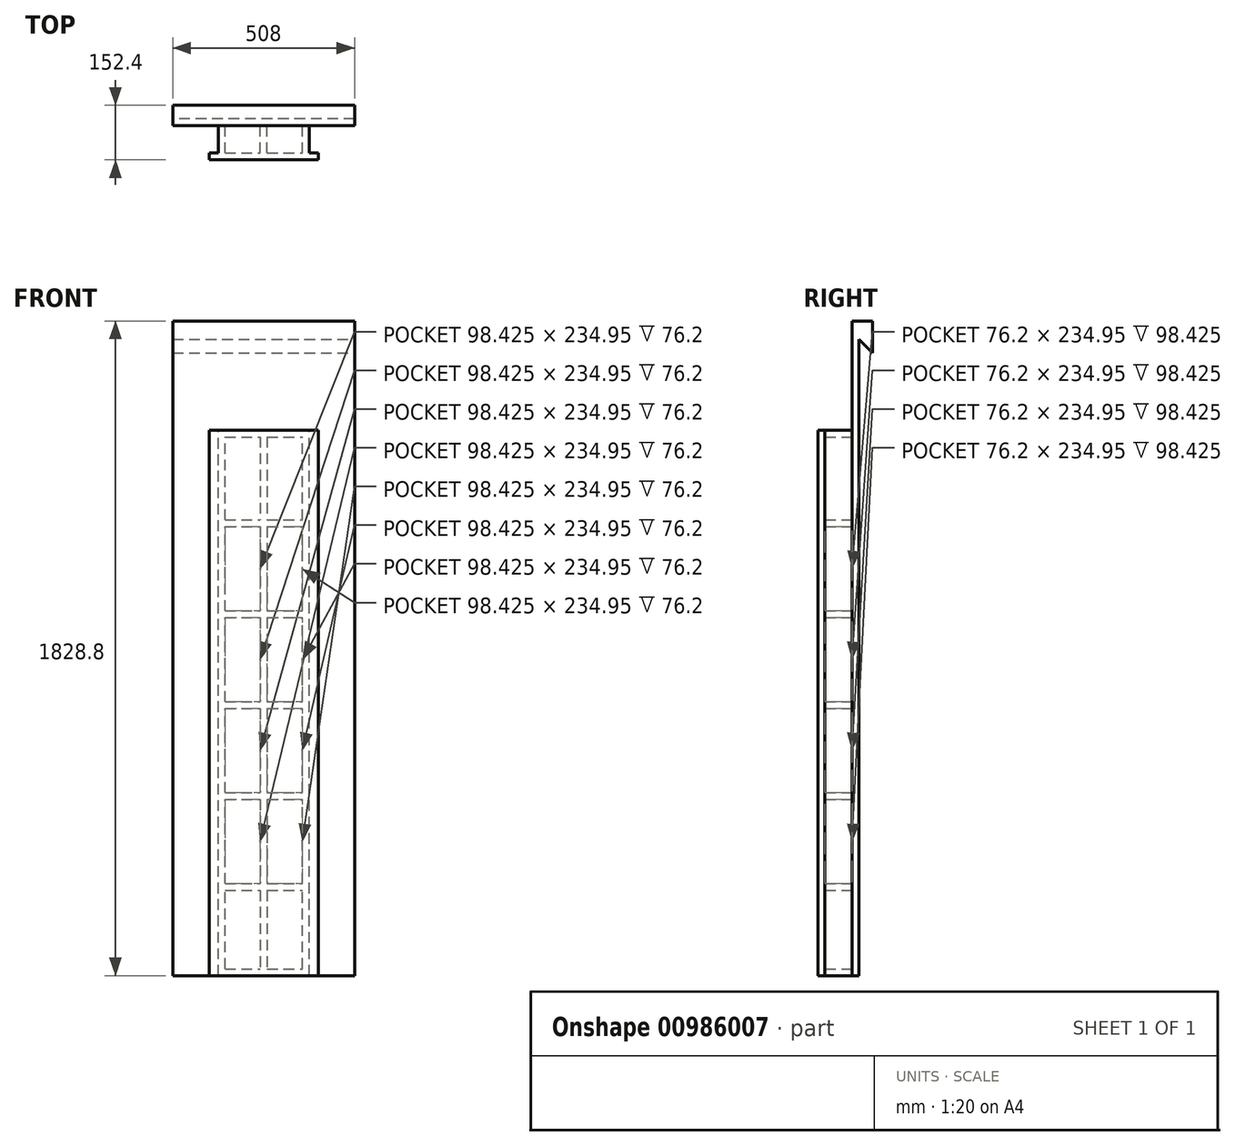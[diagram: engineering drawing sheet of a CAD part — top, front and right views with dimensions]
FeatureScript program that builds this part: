
annotation { "Feature Type Name" : "Feature", "Feature Type Description" : "" }
export const myFeature = defineFeature(function(context is Context, id is Id, definition is map)
    precondition{}
    {
        {
            var Q0;
            Q0=qCreatedBy(makeId("Front.planeOp"),FACE);
            var sketch = newSketch(context, id + "F0", { "sketchPlane" : qUnion([Q0])});
            skLineSegment(sketch, "E0.bottom", {"start": v(254, 914.4) * mm, "end": v(-254, 914.4) * mm});
            skLineSegment(sketch, "E0.top", {"start": v(254, -914.4) * mm, "end": v(-254, -914.4) * mm});
            skLineSegment(sketch, "E0.left", {"start": v(254, 914.4) * mm, "end": v(254, -914.4) * mm});
            skLineSegment(sketch, "E0.right", {"start": v(-254, 914.4) * mm, "end": v(-254, -914.4) * mm});
            skPoint(sketch, "E0.middle", {"position": v(0, 0) * mm});
            skSolve(sketch);
        }
        {
            var Q0;
            Q0=makeQuery(id+"F0.imprint","IMPRINT",FACE,{"disambiguationData":[TD([[makeQuery(id+"F0.imprint","IMPRINT",EDGE,{"derivedFrom":sQuery(id+"F0.wireOp",EDGE,"E0.bottom")}),1.0]])]});
            extrude(context, id + "F1", {"entities" : qUnion([Q0]), "depth" : 19.05 * mm, "offsetDistance" : 25.4 * mm});
        }
        {
            var Q0;
            Q0=makeQuery(id+"F1.opExtrude","CAP_FACE",FACE,{"disambiguationData":[OSD([sQuery(id+"F0.wireOp",EDGE,"E0.bottom"),sQuery(id+"F0.wireOp",EDGE,"E0.top"),sQuery(id+"F0.wireOp",EDGE,"E0.left"),sQuery(id+"F0.wireOp",EDGE,"E0.right")])],"isStart":false});
            var sketch = newSketch(context, id + "F2", { "sketchPlane" : qUnion([Q0])});
            skLineSegment(sketch, "E1.bottom", {"start": v(-127, -914.4) * mm, "end": v(127, -914.4) * mm});
            skLineSegment(sketch, "E1.top", {"start": v(-127, 609.6) * mm, "end": v(127, 609.6) * mm});
            skLineSegment(sketch, "E1.left", {"start": v(-127, -914.4) * mm, "end": v(-127, 609.6) * mm});
            skLineSegment(sketch, "E1.right", {"start": v(127, -914.4) * mm, "end": v(127, 609.6) * mm});
            skLineSegment(sketch, "E2.bottom", {"start": v(9.52, 609.6) * mm, "end": v(-9.53, 609.6) * mm});
            skLineSegment(sketch, "E2.top", {"start": v(9.52, -914.4) * mm, "end": v(-9.53, -914.4) * mm});
            skLineSegment(sketch, "E2.left", {"start": v(9.52, 590.55) * mm, "end": v(9.52, 358.78) * mm});
            skLineSegment(sketch, "E2.right", {"start": v(-9.53, 590.55) * mm, "end": v(-9.53, 358.78) * mm});
            skPoint(sketch, "E2.middle", {"position": v(0, -152.4) * mm});
            skPoint(sketch, "E2.middle.positionSnap0", {"position": v(127, -152.4) * mm});
            skPoint(sketch, "E2.centerSnap0", {"position": v(127, -152.4) * mm});
            skLineSegment(sketch, "E3.0", {"start": v(-107.95, -895.35) * mm, "end": v(-107.95, -676.28) * mm});
            skLineSegment(sketch, "E3.1", {"start": v(-107.95, -895.35) * mm, "end": v(-9.53, -895.35) * mm});
            skLineSegment(sketch, "E3.2", {"start": v(107.95, -895.35) * mm, "end": v(107.95, -676.28) * mm});
            skLineSegment(sketch, "E3.3", {"start": v(-107.95, 590.55) * mm, "end": v(-9.53, 590.55) * mm});
            skLineSegment(sketch, "E4.bottom", {"start": v(-107.95, 358.78) * mm, "end": v(-9.53, 358.78) * mm});
            skLineSegment(sketch, "E4.top", {"start": v(-107.95, 339.73) * mm, "end": v(-9.53, 339.73) * mm});
            skLineSegment(sketch, "E5.bottom", {"start": v(-107.95, 104.78) * mm, "end": v(-9.53, 104.78) * mm});
            skLineSegment(sketch, "E5.top", {"start": v(-107.95, 85.73) * mm, "end": v(-9.53, 85.73) * mm});
            skLineSegment(sketch, "E6.bottom", {"start": v(-107.95, -149.23) * mm, "end": v(-9.53, -149.23) * mm});
            skLineSegment(sketch, "E6.top", {"start": v(-107.95, -168.28) * mm, "end": v(-9.53, -168.28) * mm});
            skLineSegment(sketch, "E7.bottom", {"start": v(-107.95, -403.23) * mm, "end": v(-9.53, -403.23) * mm});
            skLineSegment(sketch, "E7.top", {"start": v(-107.95, -422.28) * mm, "end": v(-9.53, -422.28) * mm});
            skLineSegment(sketch, "E8.bottom", {"start": v(-107.95, -676.28) * mm, "end": v(-9.53, -676.28) * mm});
            skLineSegment(sketch, "E8.top", {"start": v(-107.95, -657.23) * mm, "end": v(-9.53, -657.23) * mm});
            skLineSegment(sketch, "E9.trimOffspring", {"start": v(9.52, 590.55) * mm, "end": v(107.95, 590.55) * mm});
            skLineSegment(sketch, "E10.trimOffspring", {"start": v(107.95, 358.78) * mm, "end": v(107.95, 590.55) * mm});
            skLineSegment(sketch, "E11.trimOffspring", {"start": v(-107.95, 358.78) * mm, "end": v(-107.95, 590.55) * mm});
            skLineSegment(sketch, "E12.trimOffspring", {"start": v(9.52, 358.78) * mm, "end": v(107.95, 358.78) * mm});
            skLineSegment(sketch, "E13.trimOffspring", {"start": v(9.52, 339.73) * mm, "end": v(9.52, 104.78) * mm});
            skLineSegment(sketch, "E14.trimOffspring", {"start": v(-9.53, 339.73) * mm, "end": v(-9.53, 104.78) * mm});
            skLineSegment(sketch, "E15.trimOffspring", {"start": v(9.52, 339.73) * mm, "end": v(107.95, 339.73) * mm});
            skLineSegment(sketch, "E16.trimOffspring", {"start": v(107.95, 104.78) * mm, "end": v(107.95, 339.73) * mm});
            skLineSegment(sketch, "E17.trimOffspring", {"start": v(9.52, 104.78) * mm, "end": v(107.95, 104.78) * mm});
            skLineSegment(sketch, "E18.trimOffspring", {"start": v(9.52, 85.73) * mm, "end": v(9.52, -149.23) * mm});
            skLineSegment(sketch, "E19.trimOffspring", {"start": v(9.52, 85.73) * mm, "end": v(107.95, 85.73) * mm});
            skLineSegment(sketch, "E20.trimOffspring", {"start": v(-9.53, 85.73) * mm, "end": v(-9.53, -149.23) * mm});
            skLineSegment(sketch, "E21.trimOffspring", {"start": v(-107.95, 104.78) * mm, "end": v(-107.95, 339.73) * mm});
            skLineSegment(sketch, "E22.trimOffspring", {"start": v(107.95, -149.23) * mm, "end": v(107.95, 85.73) * mm});
            skLineSegment(sketch, "E23.trimOffspring", {"start": v(9.52, -168.28) * mm, "end": v(9.52, -403.23) * mm});
            skLineSegment(sketch, "E24.trimOffspring", {"start": v(9.52, -149.23) * mm, "end": v(107.95, -149.23) * mm});
            skLineSegment(sketch, "E25.trimOffspring", {"start": v(-9.53, -168.28) * mm, "end": v(-9.53, -403.23) * mm});
            skLineSegment(sketch, "E26.trimOffspring", {"start": v(9.52, -168.28) * mm, "end": v(107.95, -168.28) * mm});
            skLineSegment(sketch, "E27.trimOffspring", {"start": v(-107.95, -149.23) * mm, "end": v(-107.95, 85.73) * mm});
            skLineSegment(sketch, "E28.trimOffspring", {"start": v(107.95, -403.23) * mm, "end": v(107.95, -168.28) * mm});
            skLineSegment(sketch, "E29.trimOffspring", {"start": v(9.52, -422.28) * mm, "end": v(9.52, -657.23) * mm});
            skLineSegment(sketch, "E30.trimOffspring", {"start": v(9.52, -422.28) * mm, "end": v(107.95, -422.28) * mm});
            skLineSegment(sketch, "E31.trimOffspring", {"start": v(9.52, -403.23) * mm, "end": v(107.95, -403.23) * mm});
            skLineSegment(sketch, "E32.trimOffspring", {"start": v(-9.53, -422.28) * mm, "end": v(-9.53, -657.23) * mm});
            skLineSegment(sketch, "E33.trimOffspring", {"start": v(-107.95, -403.23) * mm, "end": v(-107.95, -168.28) * mm});
            skLineSegment(sketch, "E34.trimOffspring", {"start": v(107.95, -657.23) * mm, "end": v(107.95, -422.28) * mm});
            skLineSegment(sketch, "E35.trimOffspring", {"start": v(9.52, -657.23) * mm, "end": v(107.95, -657.23) * mm});
            skLineSegment(sketch, "E36.trimOffspring", {"start": v(9.52, -676.28) * mm, "end": v(107.95, -676.28) * mm});
            skLineSegment(sketch, "E37.trimOffspring", {"start": v(9.52, -676.28) * mm, "end": v(9.52, -895.35) * mm});
            skLineSegment(sketch, "E38.trimOffspring", {"start": v(-9.53, -676.28) * mm, "end": v(-9.53, -895.35) * mm});
            skLineSegment(sketch, "E39.trimOffspring", {"start": v(-107.95, -657.23) * mm, "end": v(-107.95, -422.28) * mm});
            skLineSegment(sketch, "E40.trimOffspring", {"start": v(9.52, -895.35) * mm, "end": v(107.95, -895.35) * mm});
            skSolve(sketch);
        }
        {
            var Q0;
            {var subQ3=sQuery(id+"F2.wireOp",EDGE,"E1.left");Q0=makeQuery(id+"F2.imprint","IMPRINT",FACE,{"disambiguationData":[TD([[makeQuery(id+"F2.imprint","IMPRINT",EDGE,{"derivedFrom":subQ3}),-1.0]])]});}
            extrude(context, id + "F3", {"entities" : qUnion([Q0]), "operationType" : NewBodyOperationType.ADD, "depth" : 76.2 * mm, "offsetDistance" : 25.4 * mm});
        }
        {
            var Q0;
            Q0=makeQuery(id+"F3.opExtrude","CAP_FACE",FACE,{"disambiguationData":[OSD([sQuery(id+"F2.wireOp",EDGE,"E1.bottom"),sQuery(id+"F2.wireOp",EDGE,"E1.top"),sQuery(id+"F2.wireOp",EDGE,"E1.left"),sQuery(id+"F2.wireOp",EDGE,"E1.right"),sQuery(id+"F2.wireOp",EDGE,"E2.bottom"),sQuery(id+"F2.wireOp",EDGE,"E2.top"),sQuery(id+"F2.wireOp",EDGE,"E2.left"),sQuery(id+"F2.wireOp",EDGE,"E2.right"),sQuery(id+"F2.wireOp",EDGE,"E3.0"),sQuery(id+"F2.wireOp",EDGE,"E3.1"),sQuery(id+"F2.wireOp",EDGE,"E3.2"),sQuery(id+"F2.wireOp",EDGE,"E3.3"),sQuery(id+"F2.wireOp",EDGE,"E4.bottom"),sQuery(id+"F2.wireOp",EDGE,"E4.top"),sQuery(id+"F2.wireOp",EDGE,"E5.bottom"),sQuery(id+"F2.wireOp",EDGE,"E5.top"),sQuery(id+"F2.wireOp",EDGE,"E6.bottom"),sQuery(id+"F2.wireOp",EDGE,"E6.top"),sQuery(id+"F2.wireOp",EDGE,"E7.bottom"),sQuery(id+"F2.wireOp",EDGE,"E7.top"),sQuery(id+"F2.wireOp",EDGE,"E8.bottom"),sQuery(id+"F2.wireOp",EDGE,"E8.top"),sQuery(id+"F2.wireOp",EDGE,"E9.trimOffspring"),sQuery(id+"F2.wireOp",EDGE,"E10.trimOffspring"),sQuery(id+"F2.wireOp",EDGE,"E11.trimOffspring"),sQuery(id+"F2.wireOp",EDGE,"E12.trimOffspring"),sQuery(id+"F2.wireOp",EDGE,"E13.trimOffspring"),sQuery(id+"F2.wireOp",EDGE,"E14.trimOffspring"),sQuery(id+"F2.wireOp",EDGE,"E15.trimOffspring"),sQuery(id+"F2.wireOp",EDGE,"E16.trimOffspring"),sQuery(id+"F2.wireOp",EDGE,"E17.trimOffspring"),sQuery(id+"F2.wireOp",EDGE,"E18.trimOffspring"),sQuery(id+"F2.wireOp",EDGE,"E19.trimOffspring"),sQuery(id+"F2.wireOp",EDGE,"E20.trimOffspring"),sQuery(id+"F2.wireOp",EDGE,"E21.trimOffspring"),sQuery(id+"F2.wireOp",EDGE,"E22.trimOffspring"),sQuery(id+"F2.wireOp",EDGE,"E23.trimOffspring"),sQuery(id+"F2.wireOp",EDGE,"E24.trimOffspring"),sQuery(id+"F2.wireOp",EDGE,"E25.trimOffspring"),sQuery(id+"F2.wireOp",EDGE,"E26.trimOffspring"),sQuery(id+"F2.wireOp",EDGE,"E27.trimOffspring"),sQuery(id+"F2.wireOp",EDGE,"E28.trimOffspring"),sQuery(id+"F2.wireOp",EDGE,"E29.trimOffspring"),sQuery(id+"F2.wireOp",EDGE,"E30.trimOffspring"),sQuery(id+"F2.wireOp",EDGE,"E31.trimOffspring"),sQuery(id+"F2.wireOp",EDGE,"E32.trimOffspring"),sQuery(id+"F2.wireOp",EDGE,"E33.trimOffspring"),sQuery(id+"F2.wireOp",EDGE,"E34.trimOffspring"),sQuery(id+"F2.wireOp",EDGE,"E35.trimOffspring"),sQuery(id+"F2.wireOp",EDGE,"E36.trimOffspring"),sQuery(id+"F2.wireOp",EDGE,"E37.trimOffspring"),sQuery(id+"F2.wireOp",EDGE,"E38.trimOffspring"),sQuery(id+"F2.wireOp",EDGE,"E39.trimOffspring"),sQuery(id+"F2.wireOp",EDGE,"E40.trimOffspring")])],"isStart":false});
            var sketch = newSketch(context, id + "F4", { "sketchPlane" : qUnion([Q0])});
            skLineSegment(sketch, "E41.bottom", {"start": v(-152.4, -914.4) * mm, "end": v(152.4, -914.4) * mm});
            skLineSegment(sketch, "E41.top", {"start": v(-152.4, 609.6) * mm, "end": v(152.4, 609.6) * mm});
            skLineSegment(sketch, "E41.left", {"start": v(-152.4, -914.4) * mm, "end": v(-152.4, 609.6) * mm});
            skLineSegment(sketch, "E41.right", {"start": v(152.4, -914.4) * mm, "end": v(152.4, 609.6) * mm});
            skSolve(sketch);
        }
        {
            var Q0;
            Q0 = qSketchRegion(id + "F4", true);
            var Q1;
            {var subQ2=sQuery(id+"F4.wireOp",EDGE,"E41.left");Q1=makeQuery(id+"F4.imprint","IMPRINT",FACE,{"disambiguationData":[TD([[makeQuery(id+"F4.imprint","IMPRINT",EDGE,{"derivedFrom":subQ2}),-1.0]])]});}
            var Q2;
            {var subQ2=sQuery(id+"F4.wireOp",EDGE,"E41.right");Q2=makeQuery(id+"F4.imprint","IMPRINT",FACE,{"disambiguationData":[TD([[makeQuery(id+"F4.imprint","IMPRINT",EDGE,{"derivedFrom":subQ2}),1.0]])]});}
            var Q3;
            {var subQ2=makeQuery(id+"F3.opExtrude","CAP_EDGE",EDGE,{"disambiguationData":[OSD([sQuery(id+"F2.wireOp",EDGE,"E1.left")])],"isStart":false});Q3=makeQuery(id+"F4.imprint","IMPRINT",FACE,{"disambiguationData":[TD([[makeQuery(id+"F4.imprint","IMPRINT",EDGE,{"derivedFrom":subQ2}),-1.0]])]});}
            var Q4;
            Q4=makeQuery(id+"F4.imprint","IMPRINT",FACE,{"disambiguationData":[TD([[makeQuery(id+"F4.imprint","IMPRINT",EDGE,{"derivedFrom":makeQuery(id+"F3.opExtrude","CAP_EDGE",EDGE,{"disambiguationData":[OSD([sQuery(id+"F2.wireOp",EDGE,"E5.top")])],"isStart":false})}),-1.0]])]});
            var Q5;
            Q5=makeQuery(id+"F4.imprint","IMPRINT",FACE,{"disambiguationData":[TD([[makeQuery(id+"F4.imprint","IMPRINT",EDGE,{"derivedFrom":makeQuery(id+"F3.opExtrude","CAP_EDGE",EDGE,{"disambiguationData":[OSD([sQuery(id+"F2.wireOp",EDGE,"E18.trimOffspring")])],"isStart":false})}),1.0]])]});
            var Q6;
            Q6=makeQuery(id+"F4.imprint","IMPRINT",FACE,{"disambiguationData":[TD([[makeQuery(id+"F4.imprint","IMPRINT",EDGE,{"derivedFrom":makeQuery(id+"F3.opExtrude","CAP_EDGE",EDGE,{"disambiguationData":[OSD([sQuery(id+"F2.wireOp",EDGE,"E23.trimOffspring")])],"isStart":false})}),1.0]])]});
            var Q7;
            Q7=makeQuery(id+"F4.imprint","IMPRINT",FACE,{"disambiguationData":[TD([[makeQuery(id+"F4.imprint","IMPRINT",EDGE,{"derivedFrom":makeQuery(id+"F3.opExtrude","CAP_EDGE",EDGE,{"disambiguationData":[OSD([sQuery(id+"F2.wireOp",EDGE,"E6.top")])],"isStart":false})}),-1.0]])]});
            var Q8;
            Q8=makeQuery(id+"F4.imprint","IMPRINT",FACE,{"disambiguationData":[TD([[makeQuery(id+"F4.imprint","IMPRINT",EDGE,{"derivedFrom":makeQuery(id+"F3.opExtrude","CAP_EDGE",EDGE,{"disambiguationData":[OSD([sQuery(id+"F2.wireOp",EDGE,"E13.trimOffspring")])],"isStart":false})}),1.0]])]});
            var Q9;
            Q9=makeQuery(id+"F4.imprint","IMPRINT",FACE,{"disambiguationData":[TD([[makeQuery(id+"F4.imprint","IMPRINT",EDGE,{"derivedFrom":makeQuery(id+"F3.opExtrude","CAP_EDGE",EDGE,{"disambiguationData":[OSD([sQuery(id+"F2.wireOp",EDGE,"E4.top")])],"isStart":false})}),-1.0]])]});
            var Q10;
            Q10=makeQuery(id+"F4.imprint","IMPRINT",FACE,{"disambiguationData":[TD([[makeQuery(id+"F4.imprint","IMPRINT",EDGE,{"derivedFrom":makeQuery(id+"F3.opExtrude","CAP_EDGE",EDGE,{"disambiguationData":[OSD([sQuery(id+"F2.wireOp",EDGE,"E2.left")])],"isStart":false})}),1.0]])]});
            var Q11;
            Q11=makeQuery(id+"F4.imprint","IMPRINT",FACE,{"disambiguationData":[TD([[makeQuery(id+"F4.imprint","IMPRINT",EDGE,{"derivedFrom":makeQuery(id+"F3.opExtrude","CAP_EDGE",EDGE,{"disambiguationData":[OSD([sQuery(id+"F2.wireOp",EDGE,"E2.right")])],"isStart":false})}),-1.0]])]});
            var Q12;
            Q12=makeQuery(id+"F4.imprint","IMPRINT",FACE,{"disambiguationData":[TD([[makeQuery(id+"F4.imprint","IMPRINT",EDGE,{"derivedFrom":makeQuery(id+"F3.opExtrude","CAP_EDGE",EDGE,{"disambiguationData":[OSD([sQuery(id+"F2.wireOp",EDGE,"E29.trimOffspring")])],"isStart":false})}),1.0]])]});
            var Q13;
            Q13=makeQuery(id+"F4.imprint","IMPRINT",FACE,{"disambiguationData":[TD([[makeQuery(id+"F4.imprint","IMPRINT",EDGE,{"derivedFrom":makeQuery(id+"F3.opExtrude","CAP_EDGE",EDGE,{"disambiguationData":[OSD([sQuery(id+"F2.wireOp",EDGE,"E7.top")])],"isStart":false})}),-1.0]])]});
            var Q14;
            Q14=makeQuery(id+"F4.imprint","IMPRINT",FACE,{"disambiguationData":[TD([[makeQuery(id+"F4.imprint","IMPRINT",EDGE,{"derivedFrom":makeQuery(id+"F3.opExtrude","CAP_EDGE",EDGE,{"disambiguationData":[OSD([sQuery(id+"F2.wireOp",EDGE,"E3.2")])],"isStart":false})}),1.0]])]});
            var Q15;
            Q15=makeQuery(id+"F4.imprint","IMPRINT",FACE,{"disambiguationData":[TD([[makeQuery(id+"F4.imprint","IMPRINT",EDGE,{"derivedFrom":makeQuery(id+"F3.opExtrude","CAP_EDGE",EDGE,{"disambiguationData":[OSD([sQuery(id+"F2.wireOp",EDGE,"E3.0")])],"isStart":false})}),-1.0]])]});
            extrude(context, id + "F5", {"entities" : qUnion([Q0, Q1, Q2, Q3, Q4, Q5, Q6, Q7, Q8, Q9, Q10, Q11, Q12, Q13, Q14, Q15]), "operationType" : NewBodyOperationType.ADD, "depth" : 19.05 * mm, "offsetDistance" : 25.4 * mm});
        }
        {
            var Q0;
            Q0=makeQuery(id+"F1.opExtrude","SWEPT_FACE",FACE,{"disambiguationData":[OSD([sQuery(id+"F0.wireOp",EDGE,"E0.left")])]});
            var sketch = newSketch(context, id + "F6", { "sketchPlane" : qUnion([Q0])});
            skLineSegment(sketch, "E42", {"start": v(0, 914.4) * mm, "end": v(38.1, 914.4) * mm});
            skLineSegment(sketch, "E43", {"start": v(38.1, 914.4) * mm, "end": v(38.1, 825.5) * mm});
            skLineSegment(sketch, "E44", {"start": v(38.1, 825.5) * mm, "end": v(0, 863.6) * mm});
            skSolve(sketch);
        }
        {
            var Q0;
            {var subQ0=sQuery(id+"F6.wireOp",EDGE,"E42");Q0=makeQuery(id+"F6.imprint","IMPRINT",FACE,{"disambiguationData":[TD([[makeQuery(id+"F6.imprint","IMPRINT",EDGE,{"derivedFrom":subQ0}),-1.0]])]});}
            extrude(context, id + "F7", {"entities" : qUnion([Q0]), "operationType" : NewBodyOperationType.ADD, "oppositeDirection" : true, "depth" : 508 * mm, "offsetDistance" : 25.4 * mm});
        }
    });
